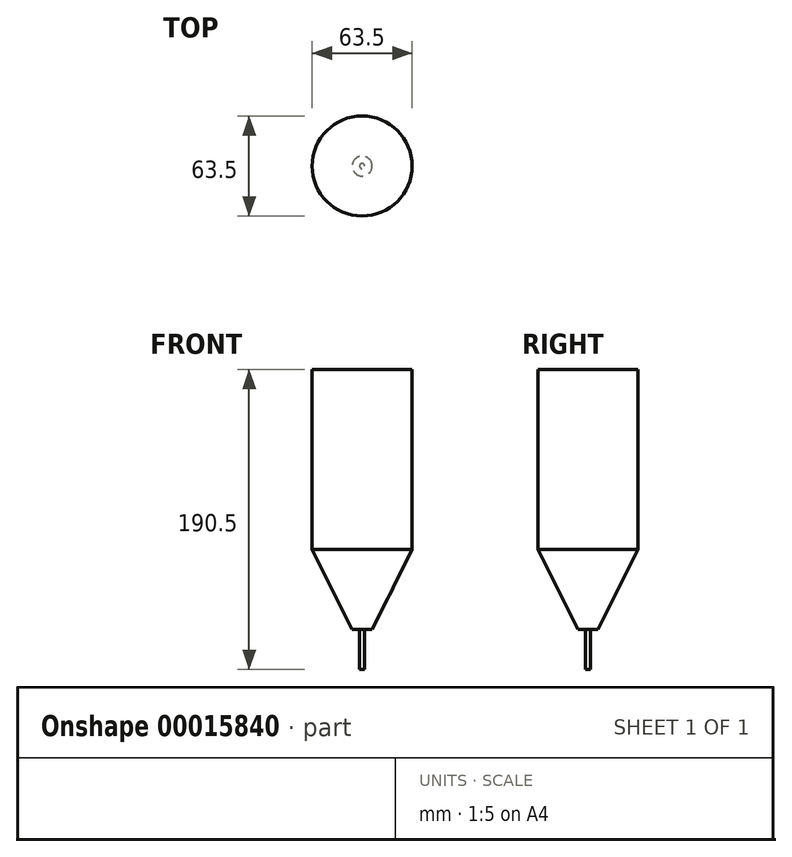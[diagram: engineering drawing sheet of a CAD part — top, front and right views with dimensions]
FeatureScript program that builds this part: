
annotation { "Feature Type Name" : "Feature", "Feature Type Description" : "" }
export const myFeature = defineFeature(function(context is Context, id is Id, definition is map)
    precondition{}
    {
        {
            var Q0;
            Q0=qCreatedBy(makeId("Top.planeOp"),FACE);
            var sketch = newSketch(context, id + "F0", { "sketchPlane" : qUnion([Q0])});
            skCircle(sketch, "E0", {"center": v(0, 0) * mm, "radius": 31.75 * mm});
            skSolve(sketch);
        }
        {
            var Q0;
            Q0 = qSketchRegion(id + "F0", true);
            extrude(context, id + "F1", {"entities" : qUnion([Q0]), "depth" : 165.1 * mm});
        }
        {
            var Q0;
            Q0=makeQuery(id+"F1.opExtrude","CAP_FACE",FACE,{"disambiguationData":[OSD([sQuery(id+"F0.wireOp",EDGE,"E0")])],"isStart":true});
            var sketch = newSketch(context, id + "F2", { "sketchPlane" : qUnion([Q0])});
            skCircle(sketch, "E1", {"center": v(0, 0) * mm, "radius": 1.59 * mm});
            skSolve(sketch);
        }
        {
            var Q0;
            Q0 = qSketchRegion(id + "F2", true);
            extrude(context, id + "F3", {"entities" : qUnion([Q0]), "operationType" : NewBodyOperationType.ADD, "depth" : 25.4 * mm});
        }
        {
            var Q0;
            Q0=makeQuery(id+"F1.opExtrude","CAP_EDGE",EDGE,{"disambiguationData":[OSD([sQuery(id+"F0.wireOp",EDGE,"E0")])],"isStart":true});
            chamfer(context, id + "F4", {"entities" : qUnion([Q0]), "chamferType" : ChamferType.TWO_OFFSETS, "width1" : 50.8 * mm, "oppositeDirection" : false, "width2" : 25.4 * mm, "tangentPropagation" : true});
        }
    });
